# Revit family: IQ8Wireless detector base
name_source: partatom
category: Fire Alarm Devices
revit_build: Autodesk Revit 2014 (Build: 20130308_1515(x64)
units: mm (PartAtom-declared; Revit-internal decimal feet)

## types (2) — shared parameters
Fire Alarm Device 01 = IQ8Quad_without_alarmdevice : O2T Multisensor Detector
Manufacturer = Esser by Honeywell
URL = http://www.esser-systems.com
content_date_modified = 16.06.2015
content_version = 1.0
h1 = 44 mm
h2 = 5 mm  [stored 0.0164042 ft]
l1 = 135 mm  [stored 0.442913 ft]
l2 = 59 mm
material = White

## per-type parameters (varying)
| type | article number |
| IQ8Wireless detector base | 805593.1 |
| IQ8Wireless gateway for devices | 805594.1 |

note: column(s) folded — value = type name in every type: Model

note: [stored X ft] marks values corroborated as IEEE doubles in the binary element streams (Revit-internal decimal feet)

## geometry (parser evidence)
native form markers: Sweep x9
no freeform markers — native parametric forms only
